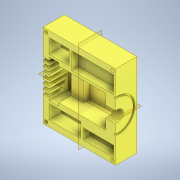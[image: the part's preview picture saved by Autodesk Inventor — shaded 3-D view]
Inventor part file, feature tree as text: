
AUTODESK INVENTOR PART (.ipt)
format: ipt  version: 2022.2 (Build 262287000, 287)  size: 373,248 bytes
history: native  units: mm
features: extrude x11, sketch x10, hole x3
ambient origin geometry x8: Origin, YZ Plane, XZ Plane, XY Plane, X Axis, Y Axis, Z Axis, Center Point
bodies: Solid1 (feature_tree)
feature tree (24):
  extrude  "MainInnerBodyExtrusion"  Depth=137.0mm
  extrude  "HoleForCameraCase"  Depth=15.7mm
  extrude  "HoleForFan"  Depth=57.0mm
  extrude  "HoleForThermister"  TaperAngle=0.0deg  [1 undecoded]
  extrude  "HoleForSensor"  Depth=62.0mm
  extrude  "SlotsForRearFan"  Depth=31.0mm
  extrude  "VentForCamera"  Depth=69.0mm
  extrude  "HoleForLens"  Depth=11.0mm
  hole  "Hole for 6-32 Insert"  [1 undecoded]
  hole  "Screw hole for 6-32 screw"  [1 undecoded]
  extrude  "HoleForLensCover"  TaperAngle=0.0deg  [1 undecoded]
  extrude  "Extrusion21"  Depth=60.0mm
  extrude  "Extrusion22"  Depth=2.0mm
  sketch  "Sketch1"  dims[d0=118.7mm d1=137.0mm]
  sketch  "Sketch3"  dims[d2=35.0mm d3=0.0mm d5=15.7mm]
  sketch  "Sketch4"  dims[d6=52.0mm d7=57.0mm]
  sketch  "Sketch10"  dims[d8=29.875mm d9=0.0mm]
  sketch  "Sketch11"  dims[d13=16.0mm d14=62.0mm]
  sketch  "Sketch15"  dims[d15=10.0mm d16=31.0mm]
  sketch  "Sketch16"  dims[d17=0.0mm d36=69.0mm]
  sketch  "Sketch18"  dims[d37=28.0mm d38=11.0mm]
  hole  "HoleFor50mmLensCover"  [1 undecoded]
  sketch  "Sketch30"  dims[d39=0.0mm d42=50.0mm]
  sketch  "Sketch31"  dims[d43=17.0mm d46=11.0mm d47=0.0mm d67=60.0mm d69=2.0mm d71=4.0mm d72=4.0mm d73=4.0mm d75=4.0mm d76=10.0mm d77=0.0mm d78=15.5mm d79=22.0mm d85=3.0mm d86=3.0mm d87=10.0mm d89=1.5mm d90=3.0mm d91=3.0mm d92=3.0mm d93=0.0mm d94=0.0mm d95=17.0mm d97=18.0mm d98=20.0mm d99=0.0mm d106=5.0mm d108=5.0mm d109=4.7mm d110=6.0mm d111=5.54mm d112=5.55mm d113=90.0deg d114=7.2mm d115=20.594885mm d116=3.797mm d117=6.0mm d118=12.7mm d119=2.362mm d120=90.0deg d121=15.0mm d122=20.594885mm d137=3.875mm d142=30.0mm d162=10.0mm d163=55.0mm d164=50.0mm d165=2.0mm d166=0.0mm d167=20.0mm d168=0.0mm d169=10.0mm d170=10.0mm d171=4.0mm d172=4.0mm d173=10.0mm d174=10.0mm d175=4.0mm d176=4.0mm d177=20.0mm d178=0.0mm]
note: 5 required parameter values undecoded (feature->parameter linkage not recoverable at this tier; creation-order binding heuristic only, values carry confidence <= 0.55)
